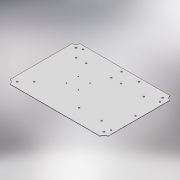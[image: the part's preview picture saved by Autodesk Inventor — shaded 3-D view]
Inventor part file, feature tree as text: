
AUTODESK INVENTOR PART (.ipt)
format: ipt  version: 2020 (Build 240168000, 168)  size: 222,208 bytes
history: native  units: mm
features: sketch x7, hole x5, extrude x2
ambient origin geometry x8: Origin, YZ Plane, XZ Plane, XY Plane, X Axis, Y Axis, Z Axis, Center Point
bodies: Solid1 (feature_tree)
feature tree (14):
  extrude  "Extrusion1"  Depth=350.0mm
  extrude  "Extrusion2"  Depth=1.0mm
  hole  "Hole1"  [1 undecoded]
  hole  "Hole2"  [1 undecoded]
  hole  "Hole3"  [1 undecoded]
  hole  "Hole4"  [1 undecoded]
  hole  "Hole5"  [1 undecoded]
  sketch  "Sketch1"  dims[d0=250.0mm d1=350.0mm]
  sketch  "Sketch2"  dims[d2=1.0mm d3=0.0mm d9=2.0mm]
  sketch  "Sketch3"  dims[d10=2.0mm d11=33.0mm]
  sketch  "Sketch5"  dims[d12=2.0mm d13=2.0mm]
  sketch  "Sketch6"  dims[d14=33.0mm d15=2.0mm]
  sketch  "Sketch7"  dims[d16=2.0mm d17=33.0mm]
  sketch  "Sketch8"  dims[d18=2.0mm d19=2.0mm d20=33.0mm d21=1.0mm d22=0.0mm d23=20.0mm d24=20.0mm d25=20.0mm d26=20.0mm d27=20.0mm d28=20.0mm d29=20.0mm d30=20.0mm d31=6.4mm d32=6.0mm d33=6.0mm d34=2.0mm d35=90.0deg d36=0.5mm d37=0.0mm d38=12.5mm d39=12.5mm d40=12.5mm d41=37.5mm d42=37.5mm d43=125.0mm d44=112.5mm d45=175.0mm d46=37.5mm d47=12.5mm d48=12.5mm d49=12.5mm d50=5.3mm d51=6.0mm d52=6.0mm d53=2.0mm d54=90.0deg d55=0.5mm d56=0.0mm d57=58.0mm d58=50.0mm d59=50.0mm d60=58.0mm d61=5.3mm d62=6.0mm d63=6.0mm d64=2.0mm d65=90.0deg d66=0.5mm d67=20.594885mm d68=139.0mm d69=139.0mm d70=50.0mm d71=50.0mm d72=5.3mm d73=6.0mm d74=6.0mm d75=2.0mm d76=90.0deg d77=0.5mm d78=20.594885mm d79=50.0mm d80=50.0mm d81=50.0mm d82=50.0mm d83=90.0mm d84=35.0mm d85=160.0mm d86=160.0mm d87=42.0mm d88=42.0mm d89=42.0mm d90=195.5mm d91=195.5mm d92=42.0mm d93=104.0mm d94=104.0mm d95=2.7mm d96=6.0mm d97=6.0mm d98=2.0mm d99=90.0deg d100=0.5mm d101=20.594885mm]
note: 5 required parameter values undecoded (feature->parameter linkage not recoverable at this tier; creation-order binding heuristic only, values carry confidence <= 0.55)
